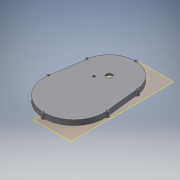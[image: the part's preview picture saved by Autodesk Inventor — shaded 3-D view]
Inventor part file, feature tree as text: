
AUTODESK INVENTOR PART (.ipt)
format: ipt  version: 2017 (Build 210142000, 142)  size: 178,688 bytes
history: native  units: mm
features: other x7, extrude x4, sketch x4, reference x3, plane x1, projected_geometry x1
ambient origin geometry x8: Origin, YZ Plane, XZ Plane, XY Plane, X Axis, Y Axis, Z Axis, Center Point
bodies: Solid1 (feature_tree)
feature tree (20):
  plane  "Work Plane1"
  extrude  "Extrusion1"  Depth=10.0mm TaperAngle=0.0deg
  extrude  "Extrusion2"  Depth=2.0mm TaperAngle=0.0deg
  extrude  "Extrusion3"  [1 undecoded]
  extrude  "Extrusion4"  [1 undecoded]
  sketch  "Sketch1"  dims[d0=10.0mm d1=0.0mm d2=10.0mm d3=0.0mm]
  reference  "Reference1"
  sketch  "Sketch2"  dims[d4=14.0mm d5=2.0mm d6=0.0mm]
  reference  "Reference2"
  sketch  "Sketch3"  dims[d7=2.0mm d8=0.0mm]
  projected_geometry  "Projected Loop1"
  sketch  "Sketch4"
  reference  "Reference3"
  parser-record x1  (decoder bookkeeping rows leaked as tree rows — omitted from the tree; the rows remain in map.json)
  other  "gearbox.iam"
  other  "case part 1:1"
  other  "case top half:1"
  other  "Spur Gears:4"
  other  "Spur Gear1:1"
  other  "case bottom half:1"
note: 2 required parameter values undecoded (feature->parameter linkage not recoverable at this tier; creation-order binding heuristic only, values carry confidence <= 0.55)
note: 1 file-system path scrubbed to <path> (originals preserved in map.json)
